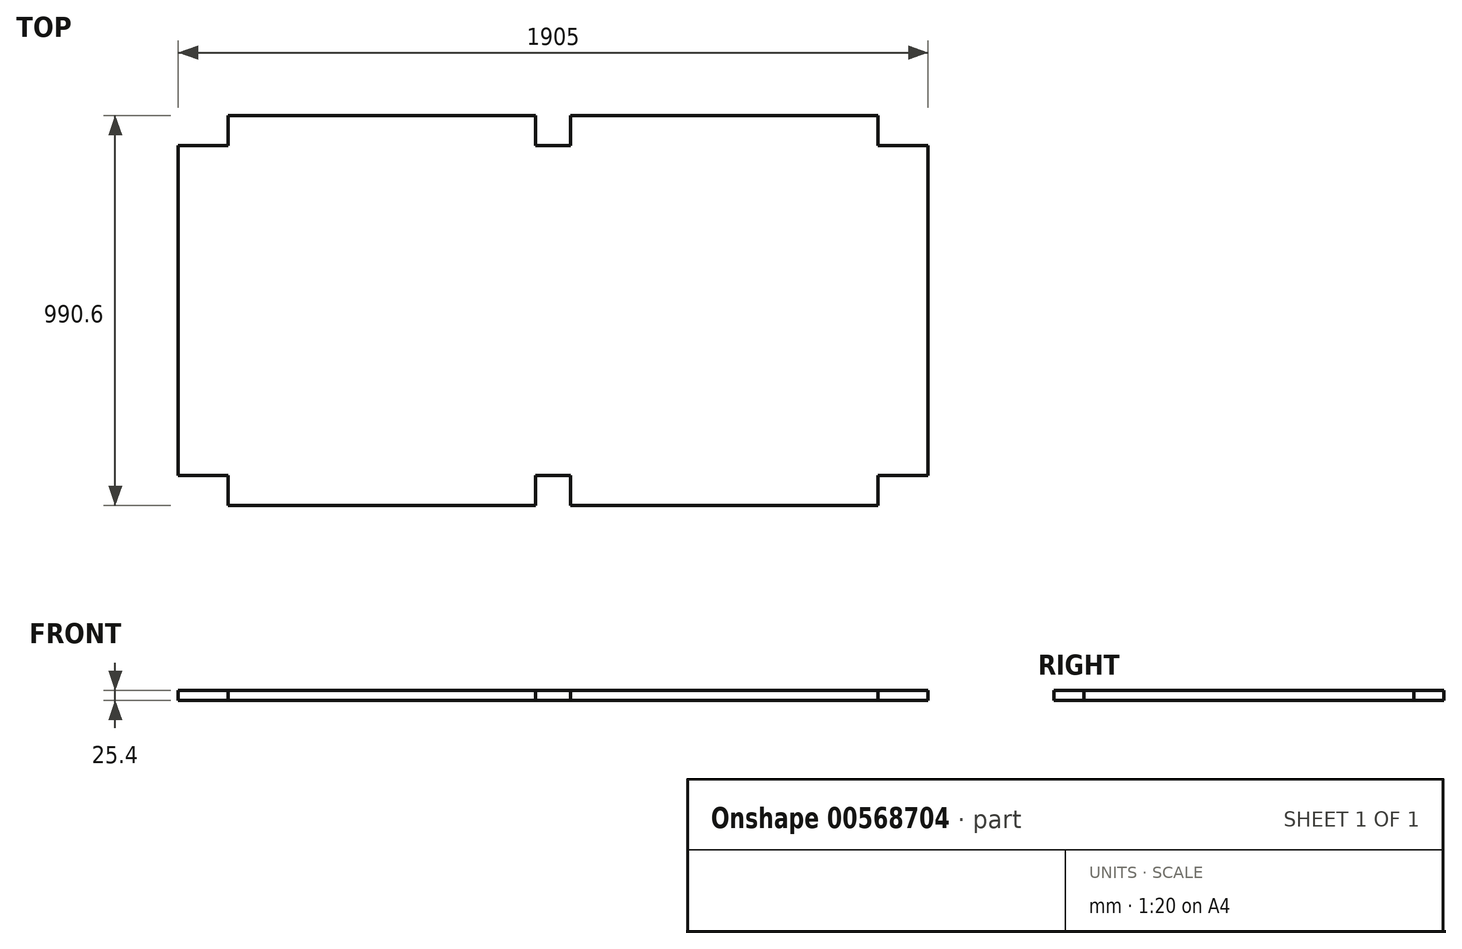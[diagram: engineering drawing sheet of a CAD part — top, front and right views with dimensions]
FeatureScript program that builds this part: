
annotation { "Feature Type Name" : "Feature", "Feature Type Description" : "" }
export const myFeature = defineFeature(function(context is Context, id is Id, definition is map)
    precondition{}
    {
        {
            var Q0;
            Q0=qCreatedBy(makeId("Front.planeOp"),FACE);
            var sketch = newSketch(context, id + "F0", { "sketchPlane" : qUnion([Q0])});
            skLineSegment(sketch, "E0.bottom", {"start": v(-952.5, 12.7) * mm, "end": v(952.5, 12.7) * mm});
            skLineSegment(sketch, "E0.top", {"start": v(-952.5, -12.7) * mm, "end": v(952.5, -12.7) * mm});
            skLineSegment(sketch, "E0.left", {"start": v(-952.5, 12.7) * mm, "end": v(-952.5, -12.7) * mm});
            skLineSegment(sketch, "E0.right", {"start": v(952.5, 12.7) * mm, "end": v(952.5, -12.7) * mm});
            skPoint(sketch, "E0.middle", {"position": v(0, 0) * mm});
            skSolve(sketch);
        }
        {
            var Q0;
            Q0 = qSketchRegion(id + "F0", true);
            extrude(context, id + "F1", {"entities" : qUnion([Q0]), "depth" : 990.6 * mm, "offsetDistance" : 25.4 * mm});
        }
        {
            var Q0;
            Q0=makeQuery(id+"F1.opExtrude","SWEPT_FACE",FACE,{"disambiguationData":[OSD([sQuery(id+"F0.wireOp",EDGE,"E0.bottom")])]});
            var sketch = newSketch(context, id + "F2", { "sketchPlane" : qUnion([Q0])});
            skLineSegment(sketch, "E1", {"start": v(-10.72, -1085.13) * mm, "end": v(0, -1085.13) * mm, "construction": true});
            skLineSegment(sketch, "E2", {"start": v(0, -1085.13) * mm, "end": v(0, 164.02) * mm, "construction": true});
            skPoint(sketch, "E3", {"position": v(0, -381) * mm});
            skLineSegment(sketch, "E4", {"start": v(0, -381) * mm, "end": v(-1277.74, -381) * mm, "construction": true});
            skLineSegment(sketch, "E5", {"start": v(-1277.74, -381) * mm, "end": v(1523.35, -381) * mm, "construction": true});
            skLineSegment(sketch, "E6.bottom", {"start": v(-952.5, 0) * mm, "end": v(-825.5, 0) * mm});
            skLineSegment(sketch, "E6.top", {"start": v(-952.5, -76.2) * mm, "end": v(-825.5, -76.2) * mm});
            skLineSegment(sketch, "E6.left", {"start": v(-952.5, 0) * mm, "end": v(-952.5, -76.2) * mm});
            skLineSegment(sketch, "E6.right", {"start": v(-825.5, 0) * mm, "end": v(-825.5, -76.2) * mm});
            skLineSegment(sketch, "E7.bottom", {"start": v(-952.5, -990.6) * mm, "end": v(-825.5, -990.6) * mm});
            skLineSegment(sketch, "E7.top", {"start": v(-952.5, -914.4) * mm, "end": v(-825.5, -914.4) * mm});
            skLineSegment(sketch, "E7.left", {"start": v(-952.5, -990.6) * mm, "end": v(-952.5, -914.4) * mm});
            skLineSegment(sketch, "E7.right", {"start": v(-825.5, -990.6) * mm, "end": v(-825.5, -914.4) * mm});
            skLineSegment(sketch, "E8.bottom", {"start": v(952.5, -990.6) * mm, "end": v(825.5, -990.6) * mm});
            skLineSegment(sketch, "E8.top", {"start": v(952.5, -914.4) * mm, "end": v(825.5, -914.4) * mm});
            skLineSegment(sketch, "E8.left", {"start": v(952.5, -990.6) * mm, "end": v(952.5, -914.4) * mm});
            skLineSegment(sketch, "E8.right", {"start": v(825.5, -990.6) * mm, "end": v(825.5, -914.4) * mm});
            skLineSegment(sketch, "E9.bottom", {"start": v(952.5, 0) * mm, "end": v(825.5, 0) * mm});
            skLineSegment(sketch, "E9.top", {"start": v(952.5, -76.2) * mm, "end": v(825.5, -76.2) * mm});
            skLineSegment(sketch, "E9.left", {"start": v(952.5, 0) * mm, "end": v(952.5, -76.2) * mm});
            skLineSegment(sketch, "E9.right", {"start": v(825.5, 0) * mm, "end": v(825.5, -76.2) * mm});
            skLineSegment(sketch, "E10.bottom", {"start": v(44.45, -76.2) * mm, "end": v(-44.45, -76.2) * mm});
            skLineSegment(sketch, "E10.top", {"start": v(44.45, 76.2) * mm, "end": v(-44.45, 76.2) * mm});
            skLineSegment(sketch, "E10.left", {"start": v(44.45, -76.2) * mm, "end": v(44.45, 76.2) * mm});
            skLineSegment(sketch, "E10.right", {"start": v(-44.45, -76.2) * mm, "end": v(-44.45, 76.2) * mm});
            skPoint(sketch, "E10.middle", {"position": v(0, 0) * mm});
            skLineSegment(sketch, "E11.bottom", {"start": v(44.45, -914.4) * mm, "end": v(-44.45, -914.4) * mm});
            skLineSegment(sketch, "E11.top", {"start": v(44.45, -1066.8) * mm, "end": v(-44.45, -1066.8) * mm});
            skLineSegment(sketch, "E11.left", {"start": v(44.45, -914.4) * mm, "end": v(44.45, -1066.8) * mm});
            skLineSegment(sketch, "E11.right", {"start": v(-44.45, -914.4) * mm, "end": v(-44.45, -1066.8) * mm});
            skPoint(sketch, "E11.middle", {"position": v(0, -990.6) * mm});
            skSolve(sketch);
        }
        {
            var Q0;
            Q0 = qSketchRegion(id + "F2", true);
            extrude(context, id + "F3", {"entities" : qUnion([Q0]), "operationType" : NewBodyOperationType.REMOVE, "oppositeDirection" : true, "depth" : 25.4 * mm, "offsetDistance" : 25.4 * mm});
        }
    });
